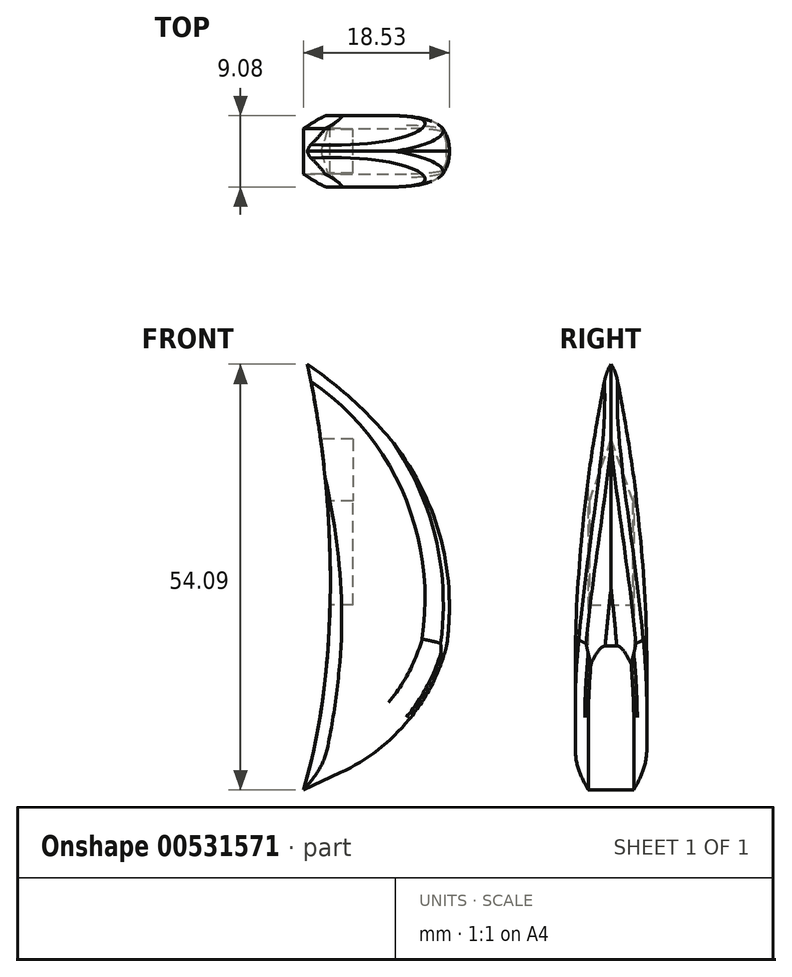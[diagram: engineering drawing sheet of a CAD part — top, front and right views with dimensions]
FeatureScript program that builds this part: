
annotation { "Feature Type Name" : "Feature", "Feature Type Description" : "" }
export const myFeature = defineFeature(function(context is Context, id is Id, definition is map)
    precondition{}
    {
        {
            var Q0;
            Q0=qCreatedBy(makeId("Front.planeOp"),FACE);
            var sketch = newSketch(context, id + "F0", { "sketchPlane" : qUnion([Q0])});
            skFitSpline(sketch, "E0", {"points": [v(0, 40.5) * mm, v(0, -27.5) * mm, v(-31.7, -77.8) * mm], "startDerivative": vector(26.09, -104.96) * mm, "endDerivative": vector(-76.1, -99.05) * mm});
            skLineSegment(sketch, "E1", {"start": v(5.72, -24.84) * mm, "end": v(0, -27.5) * mm});
            skLineSegment(sketch, "E2", {"start": v(22.5, -3.33) * mm, "end": v(21.64, -7.8) * mm});
            skArc(sketch, "E3.filletArc", {"start": v(5.72, -24.84) * mm, "mid": v(16.7, -16.1) * mm, "end": v(22.5, -3.33) * mm});
            skLineSegment(sketch, "E4", {"start": v(0, 40.5) * mm, "end": v(6.18, 35.38) * mm});
            skArc(sketch, "E5.filletArc", {"start": v(21.64, -7.8) * mm, "mid": v(19.83, 15.9) * mm, "end": v(6.18, 35.38) * mm});
            skSolve(sketch);
        }
        {
            var Q0;
            Q0=makeQuery(id+"F0.imprint","IMPRINT",FACE,{"disambiguationData":[TD([[makeQuery(id+"F0.imprint","IMPRINT",EDGE,{"derivedFrom":sQuery(id+"F0.wireOp",EDGE,"E0")}),1.0]])]});
            extrude(context, id + "F1", {"entities" : qUnion([Q0]), "depth" : 5.5 * mm, "offsetDistance" : 25 * mm});
        }
        {
            var Q0;
            Q0=makeQuery(id+"F1.opExtrude","CAP_EDGE",EDGE,{"disambiguationData":[OSD([sQuery(id+"F0.wireOp",EDGE,"E5.filletArc")])],"isStart":false});
            fillet(context, id + "F2", {"entities" : qUnion([Q0]), "radius" : 105.5 * mm, "tangentPropagation" : true, "allowEdgeOverflow" : false});
        }
        {
            var Q0;
            Q0=makeQuery(id+"F1.opExtrude","CAP_FACE",FACE,{"disambiguationData":[OSD([sQuery(id+"F0.wireOp",EDGE,"E0"),sQuery(id+"F0.wireOp",EDGE,"E1"),sQuery(id+"F0.wireOp",EDGE,"E3.filletArc"),sQuery(id+"F0.wireOp",EDGE,"E4"),sQuery(id+"F0.wireOp",EDGE,"E5.filletArc")])],"isStart":false});
            var Q1;
            Q1=makeQuery(id+"F2.opFillet","BLEND_EDGE",EDGE,{"blendedFrom":[makeQuery(id+"F1.opExtrude","CAP_EDGE",EDGE,{"disambiguationData":[OSD([sQuery(id+"F0.wireOp",EDGE,"E4")])],"isStart":false}),makeQuery(id+"F1.opExtrude","SWEPT_FACE",FACE,{"disambiguationData":[OSD([sQuery(id+"F0.wireOp",EDGE,"E5.filletArc")])]})],"blendedInto":[makeQuery(id+"F1.opExtrude","SWEPT_FACE",FACE,{"disambiguationData":[OSD([sQuery(id+"F0.wireOp",EDGE,"E5.filletArc")])]})]});
            chamfer(context, id + "F3", {"entities" : qUnion([Q0, Q1]), "width" : 2 * mm});
        }
        {
            var Q0;
            Q0=makeQuery(id+"F3.opChamfer","BLEND_EDGE",EDGE,{"blendedFrom":[makeQuery(id+"F1.opExtrude","CAP_EDGE",EDGE,{"disambiguationData":[OSD([sQuery(id+"F0.wireOp",EDGE,"E3.filletArc")])],"isStart":false}),makeQuery(id+"F2.opFillet","BLEND_FACE",FACE,{"disambiguationData":[OSD([sQuery(id+"F0.wireOp",EDGE,"E4")])]})],"blendedInto":[makeQuery(id+"F2.opFillet","BLEND_FACE",FACE,{"disambiguationData":[OSD([sQuery(id+"F0.wireOp",EDGE,"E4")])]})]});
            var Q1;
            {var subQ0=sQuery(id+"F0.wireOp",EDGE,"E4");Q1=makeQuery(id+"F3.opChamfer","BLEND_EDGE",EDGE,{"blendedFrom":[makeQuery(id+"F2.opFillet","BLEND_EDGE",EDGE,{"blendedFrom":[makeQuery(id+"F1.opExtrude","CAP_EDGE",EDGE,{"disambiguationData":[OSD([subQ0])],"isStart":false}),makeQuery(id+"F1.opExtrude","SWEPT_FACE",FACE,{"disambiguationData":[OSD([sQuery(id+"F0.wireOp",EDGE,"E5.filletArc")])]})],"blendedInto":[makeQuery(id+"F1.opExtrude","SWEPT_FACE",FACE,{"disambiguationData":[OSD([sQuery(id+"F0.wireOp",EDGE,"E5.filletArc")])]})]}),makeQuery(id+"F2.opFillet","BLEND_FACE",FACE,{"disambiguationData":[OSD([subQ0])]})],"blendedInto":[makeQuery(id+"F2.opFillet","BLEND_FACE",FACE,{"disambiguationData":[OSD([subQ0])]})]});}
            var Q2;
            {var subQ0=makeQuery(id+"F1.opExtrude","SWEPT_FACE",FACE,{"disambiguationData":[OSD([sQuery(id+"F0.wireOp",EDGE,"E5.filletArc")])]});Q2=makeQuery(id+"F3.opChamfer","BLEND_EDGE",EDGE,{"blendedFrom":[makeQuery(id+"F2.opFillet","BLEND_EDGE",EDGE,{"blendedFrom":[makeQuery(id+"F1.opExtrude","CAP_EDGE",EDGE,{"disambiguationData":[OSD([sQuery(id+"F0.wireOp",EDGE,"E4")])],"isStart":false}),subQ0],"blendedInto":[subQ0]}),subQ0],"blendedInto":[subQ0]});}
            fillet(context, id + "F4", {"entities" : qUnion([Q0, Q1, Q2]), "radius" : 5 * mm, "tangentPropagation" : true, "allowEdgeOverflow" : false});
        }
        {
            var Q0;
            Q0=makeQuery(id+"F1.opExtrude","SWEPT_BODY",BODY,{"disambiguationData":[OSD([sQuery(id+"F0.wireOp",EDGE,"E0"),sQuery(id+"F0.wireOp",EDGE,"E1"),sQuery(id+"F0.wireOp",EDGE,"E3.filletArc"),sQuery(id+"F0.wireOp",EDGE,"E4"),sQuery(id+"F0.wireOp",EDGE,"E5.filletArc")])]});
            var Q1;
            Q1=qCreatedBy(makeId("Front.planeOp"),FACE);
            mirror(context, id + "F5", {"operationType" : NewBodyOperationType.ADD, "entities" : qUnion([Q0]), "mirrorPlane" : qUnion([Q1])});
        }
        {
            var Q0;
            Q0=qCreatedBy(makeId("Right.planeOp"),FACE);
            var sketch = newSketch(context, id + "F6", { "sketchPlane" : qUnion([Q0])});
            skPoint(sketch, "E6.middle", {"position": v(0, 0) * mm});
            skLineSegment(sketch, "E7.bottom", {"start": v(-3.35, 0.96) * mm, "end": v(3.35, 0.96) * mm});
            skLineSegment(sketch, "E7.left", {"start": v(-3.35, 0.96) * mm, "end": v(-3.35, 16.96) * mm});
            skLineSegment(sketch, "E7.right", {"start": v(3.35, 0.96) * mm, "end": v(3.35, 16.96) * mm});
            skPoint(sketch, "E8", {"position": v(3.35, 16.96) * mm});
            skLineSegment(sketch, "E9", {"start": v(-3.35, 16.96) * mm, "end": v(0, 26.5) * mm});
            skLineSegment(sketch, "E10", {"start": v(0, 26.5) * mm, "end": v(3.35, 16.96) * mm});
            skSolve(sketch);
        }
        {
            var Q0;
            Q0=makeQuery(id+"F6.imprint","IMPRINT",FACE,{"disambiguationData":[TD([[makeQuery(id+"F6.imprint","IMPRINT",EDGE,{"derivedFrom":sQuery(id+"F6.wireOp",EDGE,"E7.bottom")}),1.0]])]});
            extrude(context, id + "F7", {"entities" : qUnion([Q0]), "operationType" : NewBodyOperationType.REMOVE, "depth" : 7.6 * mm, "offsetDistance" : 25 * mm});
        }
        {
            var Q0;
            Q0=makeQuery(id+"F1.opExtrude","SWEPT_BODY",BODY,{"disambiguationData":[OSD([sQuery(id+"F0.wireOp",EDGE,"E0"),sQuery(id+"F0.wireOp",EDGE,"E1"),sQuery(id+"F0.wireOp",EDGE,"E3.filletArc"),sQuery(id+"F0.wireOp",EDGE,"E4"),sQuery(id+"F0.wireOp",EDGE,"E5.filletArc")])]});
            var Q1;
            Q1=qCreatedBy(makeId("Origin.pointOp"),VERTEX);
            var Q2;
            Q2=qCreatedBy(makeId("Origin.pointOp"),VERTEX);
            transform(context, id + "F8", {"entities" : qUnion([Q0]), "transformType" : TransformType.SCALE_UNIFORMLY, "scale" : 0.82, "scalePoint" : qUnion([Q2]), "makeCopy" : false});
        }
    });
